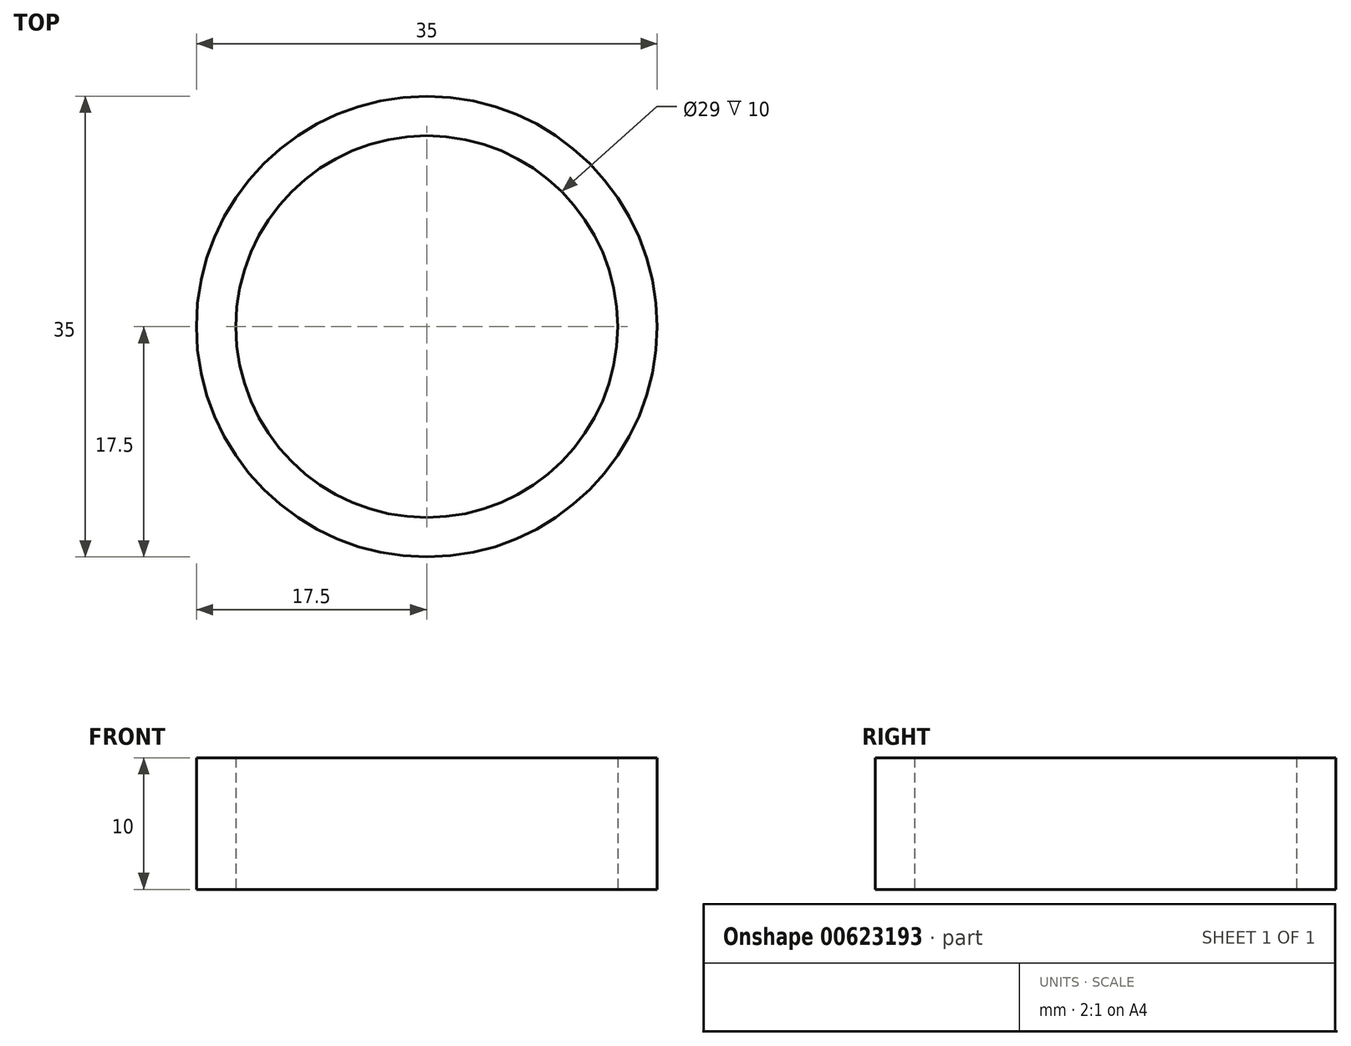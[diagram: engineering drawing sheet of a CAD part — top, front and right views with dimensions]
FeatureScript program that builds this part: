
annotation { "Feature Type Name" : "Feature", "Feature Type Description" : "" }
export const myFeature = defineFeature(function(context is Context, id is Id, definition is map)
    precondition{}
    {
        {
            var Q0;
            Q0=qCreatedBy(makeId("Top.planeOp"),FACE);
            var sketch = newSketch(context, id + "F0", { "sketchPlane" : qUnion([Q0])});
            skCircle(sketch, "E0", {"center": v(0, 0) * mm, "radius": 14.5 * mm});
            skCircle(sketch, "E1", {"center": v(0, 0) * mm, "radius": 17.5 * mm});
            skSolve(sketch);
        }
        {
            var Q0;
            Q0 = qSketchRegion(id + "F0", true);
            extrude(context, id + "F1", {"entities" : qUnion([Q0]), "depth" : 10 * mm, "offsetDistance" : 25 * mm});
        }
    });
